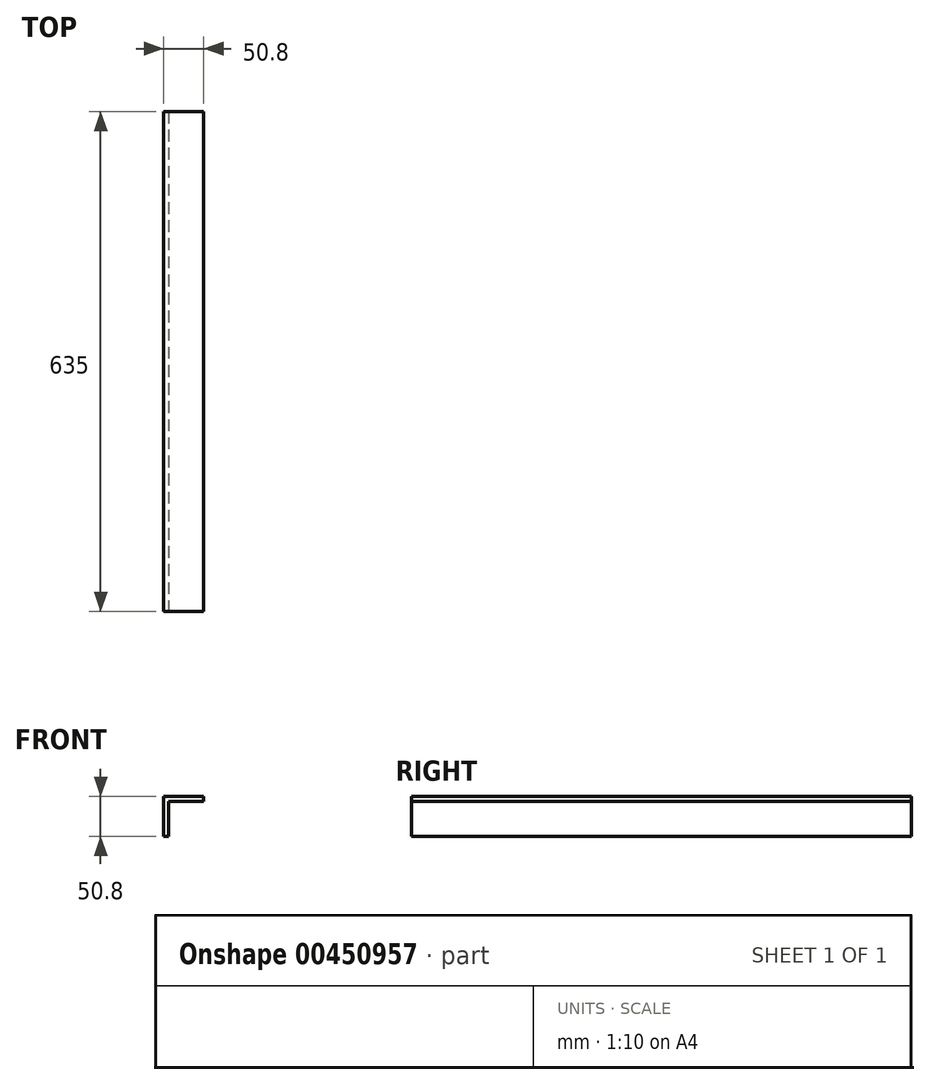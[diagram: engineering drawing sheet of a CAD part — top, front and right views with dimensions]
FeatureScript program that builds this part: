
annotation { "Feature Type Name" : "Feature", "Feature Type Description" : "" }
export const myFeature = defineFeature(function(context is Context, id is Id, definition is map)
    precondition{}
    {
        {
            var Q0;
            Q0=qCreatedBy(makeId("Front.planeOp"),FACE);
            var sketch = newSketch(context, id + "F0", { "sketchPlane" : qUnion([Q0])});
            skLineSegment(sketch, "E0", {"start": v(-27.76, 0) * mm, "end": v(-27.76, 50.8) * mm});
            skLineSegment(sketch, "E1", {"start": v(-27.76, 50.8) * mm, "end": v(23.04, 50.8) * mm});
            skLineSegment(sketch, "E2", {"start": v(23.04, 50.8) * mm, "end": v(23.04, 44.45) * mm});
            skLineSegment(sketch, "E3", {"start": v(23.04, 44.45) * mm, "end": v(-21.4, 44.45) * mm});
            skLineSegment(sketch, "E4", {"start": v(-21.4, 44.45) * mm, "end": v(-21.4, 0) * mm});
            skLineSegment(sketch, "E5", {"start": v(-21.4, 0) * mm, "end": v(-27.76, 0) * mm});
            skSolve(sketch);
        }
        {
            var Q0;
            Q0=makeQuery(id+"F0.imprint","IMPRINT",FACE,{"disambiguationData":[TD([[makeQuery(id+"F0.imprint","IMPRINT",EDGE,{"derivedFrom":sQuery(id+"F0.wireOp",EDGE,"E0")}),-1.0]])]});
            extrude(context, id + "F1", {"entities" : qUnion([Q0]), "oppositeDirection" : true, "depth" : 635 * mm});
        }
    });
